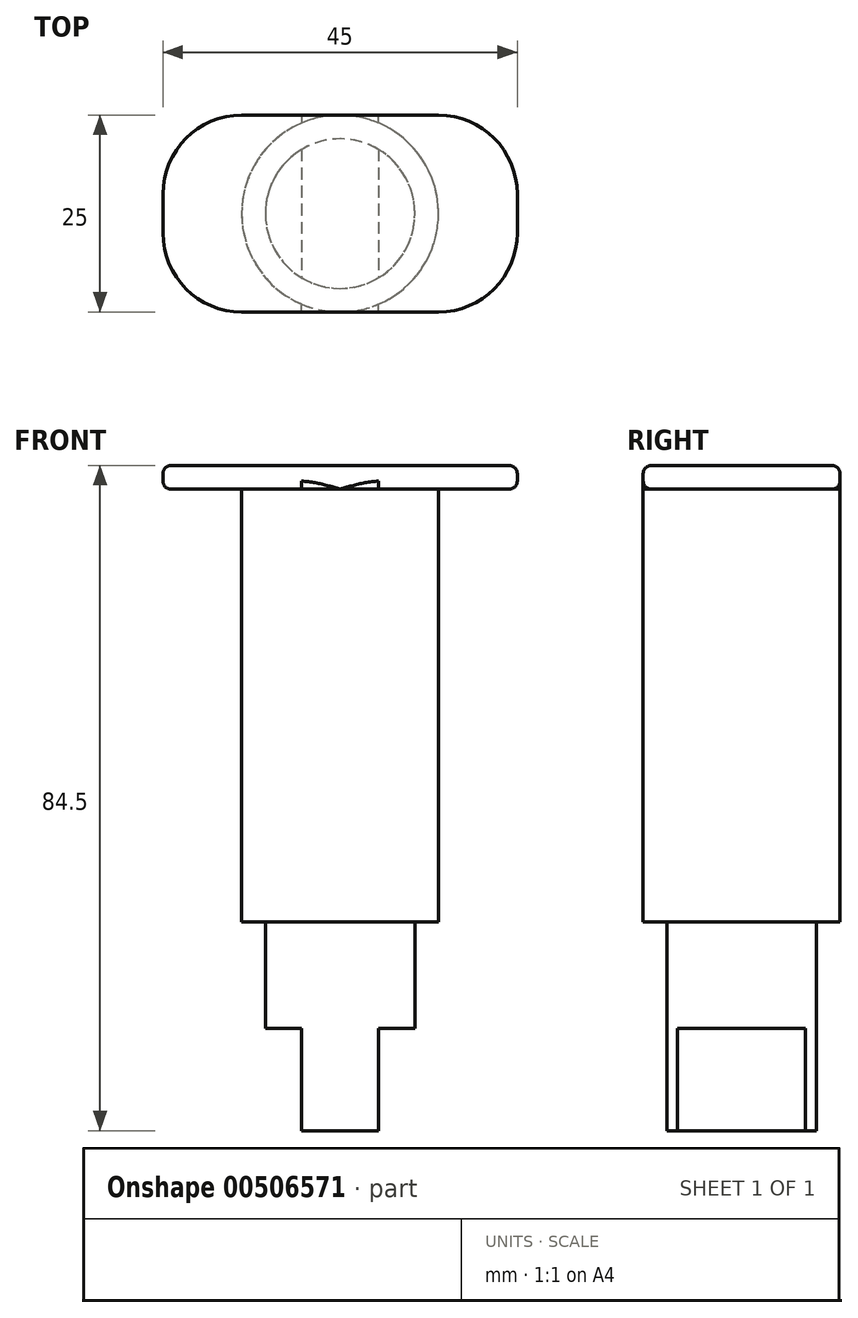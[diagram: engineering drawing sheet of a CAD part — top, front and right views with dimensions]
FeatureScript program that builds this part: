
annotation { "Feature Type Name" : "Feature", "Feature Type Description" : "" }
export const myFeature = defineFeature(function(context is Context, id is Id, definition is map)
    precondition{}
    {
        {
            var Q0;
            Q0=qCreatedBy(makeId("Top.planeOp"),FACE);
            var sketch = newSketch(context, id + "F0", { "sketchPlane" : qUnion([Q0])});
            skCircle(sketch, "E0", {"center": v(0, 0) * mm, "radius": 12.5 * mm});
            skSolve(sketch);
        }
        {
            var Q0;
            Q0=makeQuery(id+"F0.imprint","IMPRINT",FACE,{"disambiguationData":[TD([[makeQuery(id+"F0.imprint","IMPRINT",EDGE,{"derivedFrom":sQuery(id+"F0.wireOp",EDGE,"E0")}),1.0]])]});
            extrude(context, id + "F1", {"entities" : qUnion([Q0]), "depth" : 55 * mm});
        }
        {
            var Q0;
            Q0=makeQuery(id+"F1.opExtrude","CAP_FACE",FACE,{"disambiguationData":[OSD([sQuery(id+"F0.wireOp",EDGE,"E0")])],"isStart":true});
            var sketch = newSketch(context, id + "F2", { "sketchPlane" : qUnion([Q0])});
            skCircle(sketch, "E1", {"center": v(0, 0) * mm, "radius": 9.5 * mm});
            skSolve(sketch);
        }
        {
            var Q0;
            Q0=makeQuery(id+"F2.imprint","IMPRINT",FACE,{"disambiguationData":[TD([[makeQuery(id+"F2.imprint","IMPRINT",EDGE,{"derivedFrom":sQuery(id+"F2.wireOp",EDGE,"E1")}),1.0]])]});
            extrude(context, id + "F3", {"entities" : qUnion([Q0]), "operationType" : NewBodyOperationType.ADD, "depth" : 13.5 * mm});
        }
        {
            var Q0;
            Q0=makeQuery(id+"F3.opExtrude","CAP_FACE",FACE,{"disambiguationData":[OSD([sQuery(id+"F2.wireOp",EDGE,"E1")])],"isStart":false});
            var sketch = newSketch(context, id + "F4", { "sketchPlane" : qUnion([Q0])});
            skCircle(sketch, "E2", {"center": v(0, 0) * mm, "radius": 9.5 * mm});
            skLineSegment(sketch, "E3.left", {"start": v(4.9, -8.14) * mm, "end": v(4.9, 8.14) * mm});
            skLineSegment(sketch, "E3.right", {"start": v(-4.9, -8.14) * mm, "end": v(-4.9, 8.14) * mm});
            skSolve(sketch);
        }
        {
            var Q0;
            {var subQ0=sQuery(id+"F4.wireOp",EDGE,"E3.left");Q0=makeQuery(id+"F4.imprint","IMPRINT",FACE,{"disambiguationData":[TD([[makeQuery(id+"F4.imprint","IMPRINT",EDGE,{"derivedFrom":subQ0}),1.0]])]});}
            extrude(context, id + "F5", {"entities" : qUnion([Q0]), "operationType" : NewBodyOperationType.ADD, "depth" : 13 * mm});
        }
        {
            var Q0;
            Q0=makeQuery(id+"F1.opExtrude","CAP_FACE",FACE,{"disambiguationData":[OSD([sQuery(id+"F0.wireOp",EDGE,"E0")])],"isStart":false});
            var sketch = newSketch(context, id + "F6", { "sketchPlane" : qUnion([Q0])});
            skLineSegment(sketch, "E4.bottom", {"start": v(12.5, 12.5) * mm, "end": v(-12.5, 12.5) * mm});
            skLineSegment(sketch, "E4.top", {"start": v(12.5, -12.5) * mm, "end": v(-12.5, -12.5) * mm});
            skLineSegment(sketch, "E4.left", {"start": v(22.5, 2.5) * mm, "end": v(22.5, -2.5) * mm});
            skLineSegment(sketch, "E4.right", {"start": v(-22.5, 2.5) * mm, "end": v(-22.5, -2.5) * mm});
            skPoint(sketch, "E4.middle", {"position": v(0, 0) * mm});
            skPoint(sketch, "E5.visualSharp", {"position": v(22.5, 12.5) * mm});
            skArc(sketch, "E5.filletArc", {"start": v(22.5, 2.5) * mm, "mid": v(19.57, 9.57) * mm, "end": v(12.5, 12.5) * mm});
            skPoint(sketch, "E6.visualSharp", {"position": v(22.5, -12.5) * mm});
            skArc(sketch, "E6.filletArc", {"start": v(12.5, -12.5) * mm, "mid": v(19.57, -9.57) * mm, "end": v(22.5, -2.5) * mm});
            skPoint(sketch, "E7.visualSharp", {"position": v(-22.5, -12.5) * mm});
            skArc(sketch, "E7.filletArc", {"start": v(-22.5, -2.5) * mm, "mid": v(-19.57, -9.57) * mm, "end": v(-12.5, -12.5) * mm});
            skPoint(sketch, "E8.visualSharp", {"position": v(-22.5, 12.5) * mm});
            skArc(sketch, "E8.filletArc", {"start": v(-12.5, 12.5) * mm, "mid": v(-19.57, 9.57) * mm, "end": v(-22.5, 2.5) * mm});
            skSolve(sketch);
        }
        {
            var Q0;
            Q0=makeQuery(id+"F6.imprint","IMPRINT",FACE,{"disambiguationData":[TD([[makeQuery(id+"F6.imprint","IMPRINT",EDGE,{"derivedFrom":sQuery(id+"F6.wireOp",EDGE,"E4.left")}),-1.0]])]});
            var Q1;
            Q1=makeQuery(id+"F6.imprint","IMPRINT",FACE,{"disambiguationData":[TD([[makeQuery(id+"F6.imprint","IMPRINT",EDGE,{"derivedFrom":sQuery(id+"F6.wireOp",EDGE,"E4.right")}),1.0]])]});
            var Q2;
            {var subQ0=makeQuery(id+"F1.opExtrude","CAP_EDGE",EDGE,{"disambiguationData":[OSD([sQuery(id+"F0.wireOp",EDGE,"E0")])],"isStart":false});var subQ1=makeQuery(id+"F6.imprint","INTERSECT",VERTEX,{"derivedFrom":[subQ0,sQuery(id+"F6.wireOp",EDGE,"E4.bottom")]});Q2=makeQuery(id+"F6.imprint","IMPRINT",FACE,{"disambiguationData":[TD([[makeQuery(id+"F6.imprint","IMPRINT",EDGE,{"disambiguationData":[TD([[subQ1,1.0]])],"derivedFrom":subQ0}),1.0]])]});}
            extrude(context, id + "F7", {"entities" : qUnion([Q0, Q1, Q2]), "operationType" : NewBodyOperationType.ADD, "depth" : 3 * mm});
        }
        {
            var Q0;
            Q0=makeQuery(id+"F7.opExtrude","CAP_FACE",FACE,{"disambiguationData":[OSD([sQuery(id+"F6.wireOp",EDGE,"E4.bottom"),sQuery(id+"F6.wireOp",EDGE,"E4.top"),sQuery(id+"F6.wireOp",EDGE,"E4.left"),sQuery(id+"F6.wireOp",EDGE,"E4.right"),sQuery(id+"F6.wireOp",EDGE,"E5.filletArc"),sQuery(id+"F6.wireOp",EDGE,"E6.filletArc"),sQuery(id+"F6.wireOp",EDGE,"E7.filletArc"),sQuery(id+"F6.wireOp",EDGE,"E8.filletArc")])],"isStart":false});
            var Q1;
            Q1=makeQuery(id+"F7.opExtrude","CAP_EDGE",EDGE,{"disambiguationData":[OSD([sQuery(id+"F6.wireOp",EDGE,"E5.filletArc")])],"isStart":true});
            fillet(context, id + "F8", {"entities" : qUnion([Q0, Q1]), "radius" : 1 * mm, "tangentPropagation" : true, "allowEdgeOverflow" : false});
        }
    });
